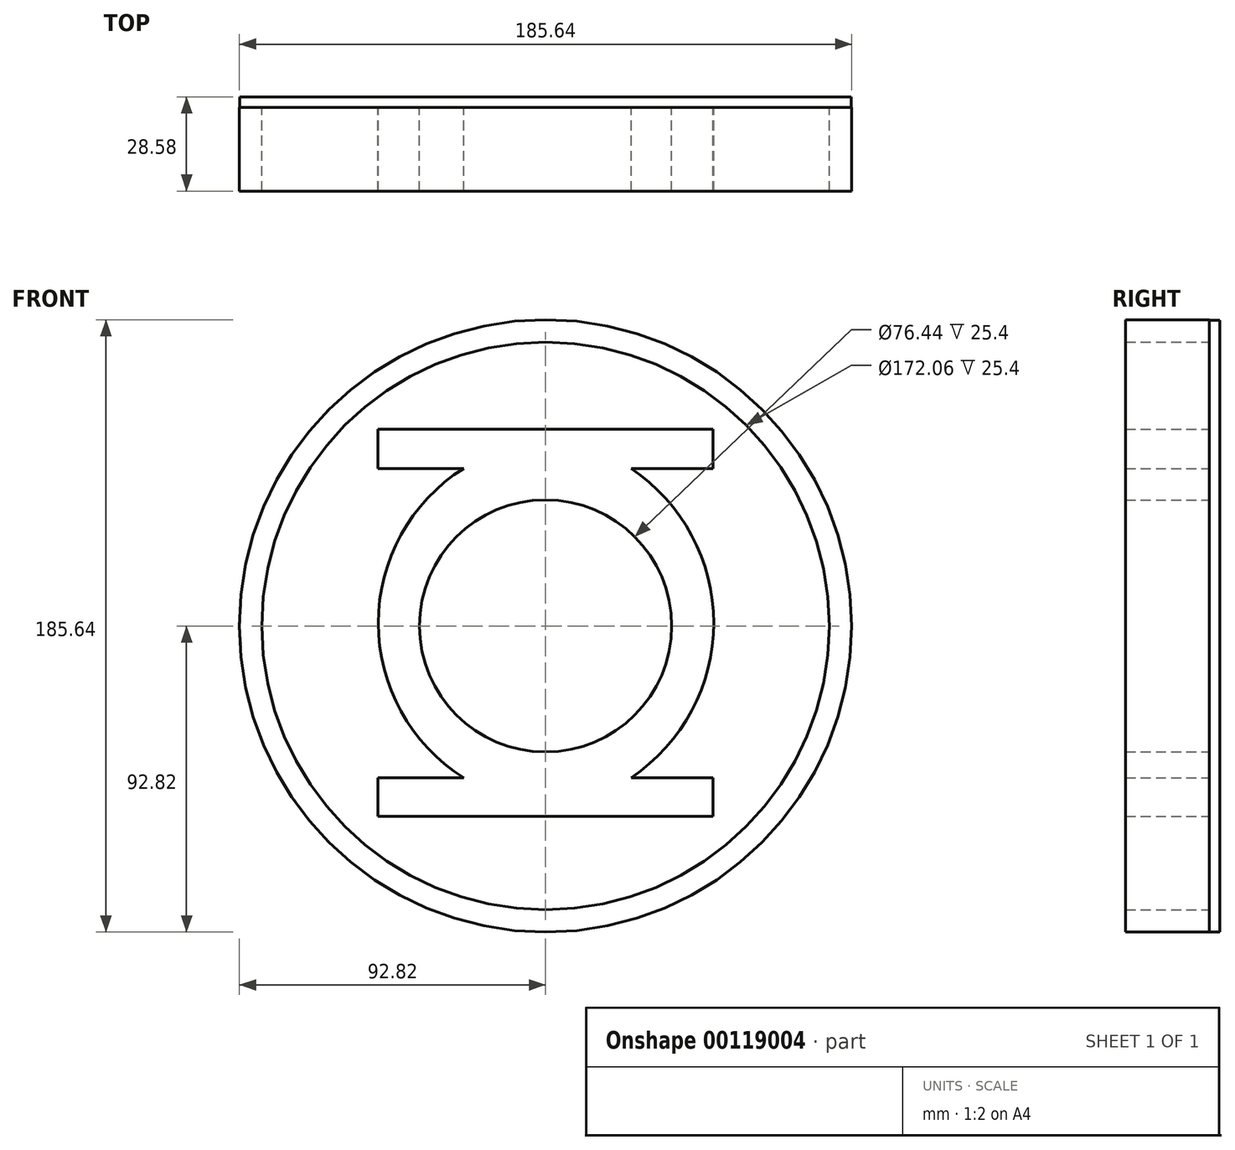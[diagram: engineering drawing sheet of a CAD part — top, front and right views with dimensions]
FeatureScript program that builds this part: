
annotation { "Feature Type Name" : "Feature", "Feature Type Description" : "" }
export const myFeature = defineFeature(function(context is Context, id is Id, definition is map)
    precondition{}
    {
        {
            var Q0;
            Q0=qCreatedBy(makeId("Front.planeOp"),FACE);
            var sketch = newSketch(context, id + "F0", { "sketchPlane" : qUnion([Q0])});
            skLineSegment(sketch, "E0", {"start": v(-50.8, 59.66) * mm, "end": v(-50.8, 47.72) * mm});
            skLineSegment(sketch, "E1", {"start": v(-50.8, 47.72) * mm, "end": v(-24.85, 47.72) * mm});
            skLineSegment(sketch, "E2", {"start": v(-50.8, 59.66) * mm, "end": v(50.8, 59.66) * mm});
            skLineSegment(sketch, "E3", {"start": v(50.8, 59.66) * mm, "end": v(50.8, 47.72) * mm});
            skLineSegment(sketch, "E4", {"start": v(50.8, 47.72) * mm, "end": v(25.95, 47.72) * mm});
            skLineSegment(sketch, "E5", {"start": v(-24.85, -46) * mm, "end": v(-50.8, -46) * mm});
            skLineSegment(sketch, "E6", {"start": v(-50.8, -46) * mm, "end": v(-50.8, -57.69) * mm});
            skLineSegment(sketch, "E7", {"start": v(-50.8, -57.69) * mm, "end": v(50.8, -57.69) * mm});
            skLineSegment(sketch, "E8", {"start": v(50.8, -57.69) * mm, "end": v(50.8, -46) * mm});
            skLineSegment(sketch, "E9", {"start": v(50.8, -46) * mm, "end": v(25.95, -46) * mm});
            skArc(sketch, "E10", {"start": v(-24.85, 47.72) * mm, "mid": v(-50.72, 0.86) * mm, "end": v(-24.85, -46) * mm});
            skArc(sketch, "E11", {"start": v(25.95, -46) * mm, "mid": v(50.98, 0.86) * mm, "end": v(25.95, 47.72) * mm});
            skCircle(sketch, "E12", {"center": v(0, 0) * mm, "radius": 38.22 * mm});
            skCircle(sketch, "E13", {"center": v(0, 0) * mm, "radius": 86.03 * mm});
            skCircle(sketch, "E14", {"center": v(0, 0) * mm, "radius": 92.82 * mm});
            skSolve(sketch);
        }
        {
            var Q0;
            Q0=makeQuery(id+"F0.imprint","IMPRINT",FACE,{"disambiguationData":[TD([[makeQuery(id+"F0.imprint","IMPRINT",EDGE,{"derivedFrom":sQuery(id+"F0.wireOp",EDGE,"E13")}),-1.0]])]});
            var Q1;
            Q1=makeQuery(id+"F0.imprint","IMPRINT",FACE,{"disambiguationData":[TD([[makeQuery(id+"F0.imprint","IMPRINT",EDGE,{"derivedFrom":sQuery(id+"F0.wireOp",EDGE,"E0")}),1.0]])]});
            extrude(context, id + "F1", {"entities" : qUnion([Q0, Q1]), "depth" : 25.4 * mm});
        }
        {
            var Q0;
            Q0=makeQuery(id+"F1.opExtrude","CAP_FACE",FACE,{"disambiguationData":[OSD([sQuery(id+"F0.wireOp",EDGE,"E0"),sQuery(id+"F0.wireOp",EDGE,"E1"),sQuery(id+"F0.wireOp",EDGE,"E2"),sQuery(id+"F0.wireOp",EDGE,"E3"),sQuery(id+"F0.wireOp",EDGE,"E4"),sQuery(id+"F0.wireOp",EDGE,"E5"),sQuery(id+"F0.wireOp",EDGE,"E6"),sQuery(id+"F0.wireOp",EDGE,"E7"),sQuery(id+"F0.wireOp",EDGE,"E8"),sQuery(id+"F0.wireOp",EDGE,"E9"),sQuery(id+"F0.wireOp",EDGE,"E10"),sQuery(id+"F0.wireOp",EDGE,"E11"),sQuery(id+"F0.wireOp",EDGE,"E12")])],"isStart":true});
            var sketch = newSketch(context, id + "F2", { "sketchPlane" : qUnion([Q0])});
            skCircle(sketch, "E15", {"center": v(0, 0) * mm, "radius": 92.7 * mm});
            skSolve(sketch);
        }
        {
            var Q0;
            Q0 = qSketchRegion(id + "F2", true);
            extrude(context, id + "F3", {"entities" : qUnion([Q0]), "depth" : 3.17 * mm});
        }
    });
